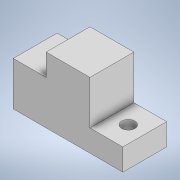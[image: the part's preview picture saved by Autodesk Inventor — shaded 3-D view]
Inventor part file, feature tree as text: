
AUTODESK INVENTOR PART (.ipt)
format: ipt  version: 2021 (Build 250183000, 183)  size: 112,640 bytes
history: native  units: mm
features: sketch x2, other x1, extrude x1, hole x1
ambient origin geometry x8: Origin, YZ Plane, XZ Plane, XY Plane, X Axis, Y Axis, Z Axis, Center Point
bodies: Body1 (feature_tree)
feature tree (5):
  other  "Sólido1"
  extrude  "Extrusão1"  Depth=10.0mm
  hole  "Furo1"  [1 undecoded]
  sketch  "Esboço1"  dims[d0=50.0mm d1=10.0mm]
  sketch  "Esboço2"  dims[d2=20.0mm d3=15.0mm d4=10.0mm d5=20.0mm d6=20.0mm d7=0.0mm d8=7.5mm d9=6.0mm d10=6.0mm d11=4.0mm d12=2.0mm d13=90.0deg d14=8.0mm d15=20.594885mm d16=10.0mm d17=1.0mm d18=1.0mm d19=0.15mm d20=0.25mm d21=0.375mm d22=14.3117mm d23=0.75mm d24=20.594885mm d25=0.0625mm d26=0.75mm d27=0.375mm]
note: 1 required parameter value undecoded (feature->parameter linkage not recoverable at this tier; creation-order binding heuristic only, values carry confidence <= 0.55)
